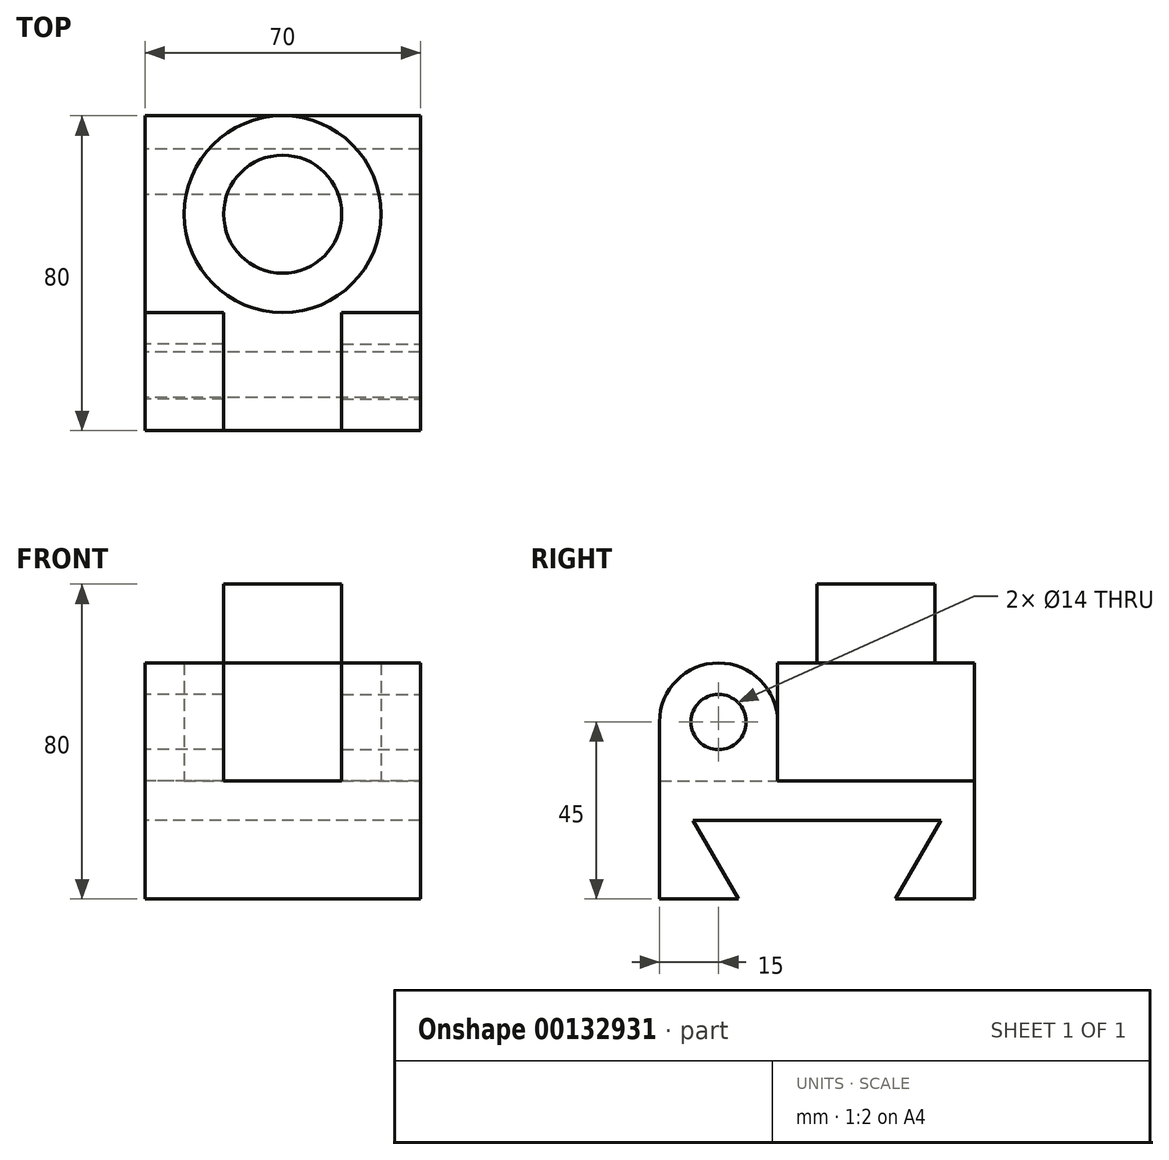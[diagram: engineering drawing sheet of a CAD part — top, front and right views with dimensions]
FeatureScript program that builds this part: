
annotation { "Feature Type Name" : "Feature", "Feature Type Description" : "" }
export const myFeature = defineFeature(function(context is Context, id is Id, definition is map)
    precondition{}
    {
        {
            var Q0;
            Q0=qCreatedBy(makeId("Right.planeOp"),FACE);
            var sketch = newSketch(context, id + "F0", { "sketchPlane" : qUnion([Q0])});
            skLineSegment(sketch, "E0", {"start": v(-20, 0) * mm, "end": v(-40, 0) * mm});
            skLineSegment(sketch, "E1", {"start": v(-40, 0) * mm, "end": v(-40, 30) * mm});
            skLineSegment(sketch, "E2", {"start": v(-40, 30) * mm, "end": v(40, 30) * mm});
            skLineSegment(sketch, "E3", {"start": v(40, 30) * mm, "end": v(40, 0) * mm});
            skLineSegment(sketch, "E4", {"start": v(40, 0) * mm, "end": v(20, 0) * mm});
            skLineSegment(sketch, "E5", {"start": v(20, 0) * mm, "end": v(31.55, 20) * mm});
            skLineSegment(sketch, "E6", {"start": v(31.55, 20) * mm, "end": v(-31.55, 20) * mm});
            skLineSegment(sketch, "E7", {"start": v(-31.55, 20) * mm, "end": v(-20, 0) * mm});
            skSolve(sketch);
        }
        {
            var Q0;
            Q0=makeQuery(id+"F0.imprint","IMPRINT",FACE,{"disambiguationData":[TD([[makeQuery(id+"F0.imprint","IMPRINT",EDGE,{"derivedFrom":sQuery(id+"F0.wireOp",EDGE,"E0")}),-1.0]])]});
            extrude(context, id + "F1", {"entities" : qUnion([Q0]), "endBound" : BoundingType.SYMMETRIC, "depth" : 70 * mm});
        }
        {
            var Q0;
            Q0=makeQuery(id+"F1.opExtrude","CAP_FACE",FACE,{"disambiguationData":[OSD([sQuery(id+"F0.wireOp",EDGE,"E0"),sQuery(id+"F0.wireOp",EDGE,"E1"),sQuery(id+"F0.wireOp",EDGE,"E2"),sQuery(id+"F0.wireOp",EDGE,"E3"),sQuery(id+"F0.wireOp",EDGE,"E4"),sQuery(id+"F0.wireOp",EDGE,"E5"),sQuery(id+"F0.wireOp",EDGE,"E6"),sQuery(id+"F0.wireOp",EDGE,"E7")])],"isStart":false});
            var sketch = newSketch(context, id + "F2", { "sketchPlane" : qUnion([Q0])});
            skCircle(sketch, "E8", {"center": v(-25, 45) * mm, "radius": 7 * mm});
            skArc(sketch, "E9", {"start": v(-10, 45) * mm, "mid": v(-25, 60) * mm, "end": v(-40, 45) * mm});
            skLineSegment(sketch, "E10", {"start": v(-40, 30) * mm, "end": v(-40, 45) * mm});
            skLineSegment(sketch, "E11", {"start": v(-10, 45) * mm, "end": v(-10, 30) * mm});
            skSolve(sketch);
        }
        {
            var Q0;
            Q0=makeQuery(id+"F2.imprint","IMPRINT",FACE,{"disambiguationData":[TD([[makeQuery(id+"F2.imprint","IMPRINT",EDGE,{"derivedFrom":sQuery(id+"F2.wireOp",EDGE,"E8")}),-1.0]])]});
            extrude(context, id + "F3", {"entities" : qUnion([Q0]), "oppositeDirection" : true, "depth" : 20 * mm});
        }
        {
            var Q0;
            Q0=makeQuery(id+"F3.opExtrude","SWEPT_BODY",BODY,{"disambiguationData":[OSD([sQuery(id+"F0.wireOp",EDGE,"E2"),sQuery(id+"F2.wireOp",EDGE,"E8"),sQuery(id+"F2.wireOp",EDGE,"E9"),sQuery(id+"F2.wireOp",EDGE,"E10"),sQuery(id+"F2.wireOp",EDGE,"E11")])]});
            var Q1;
            Q1=qCreatedBy(makeId("Right.planeOp"),FACE);
            mirror(context, id + "F4", {"operationType" : NewBodyOperationType.ADD, "entities" : qUnion([Q0]), "mirrorPlane" : qUnion([Q1])});
        }
        {
            var Q0;
            Q0=makeQuery(id+"F1.opExtrude","SWEPT_FACE",FACE,{"disambiguationData":[OSD([sQuery(id+"F0.wireOp",EDGE,"E2")])]});
            var sketch = newSketch(context, id + "F5", { "sketchPlane" : qUnion([Q0])});
            skCircle(sketch, "E12", {"center": v(0, 15) * mm, "radius": 25 * mm});
            skSolve(sketch);
        }
        {
            var Q0;
            Q0=makeQuery(id+"F5.imprint","IMPRINT",FACE,{"disambiguationData":[TD([[makeQuery(id+"F5.imprint","IMPRINT",EDGE,{"derivedFrom":sQuery(id+"F5.wireOp",EDGE,"E12")}),1.0]])]});
            extrude(context, id + "F6", {"entities" : qUnion([Q0]), "operationType" : NewBodyOperationType.ADD, "depth" : 30 * mm});
        }
        {
            var Q0;
            Q0=makeQuery(id+"F6.opExtrude","CAP_FACE",FACE,{"disambiguationData":[OSD([sQuery(id+"F5.wireOp",EDGE,"E12")])],"isStart":false});
            var sketch = newSketch(context, id + "F7", { "sketchPlane" : qUnion([Q0])});
            skCircle(sketch, "E13", {"center": v(0, 15) * mm, "radius": 15 * mm});
            skSolve(sketch);
        }
        {
            var Q0;
            Q0=makeQuery(id+"F7.imprint","IMPRINT",FACE,{"disambiguationData":[TD([[makeQuery(id+"F7.imprint","IMPRINT",EDGE,{"derivedFrom":sQuery(id+"F7.wireOp",EDGE,"E13")}),1.0]])]});
            extrude(context, id + "F8", {"entities" : qUnion([Q0]), "operationType" : NewBodyOperationType.ADD, "depth" : 20 * mm});
        }
    });
